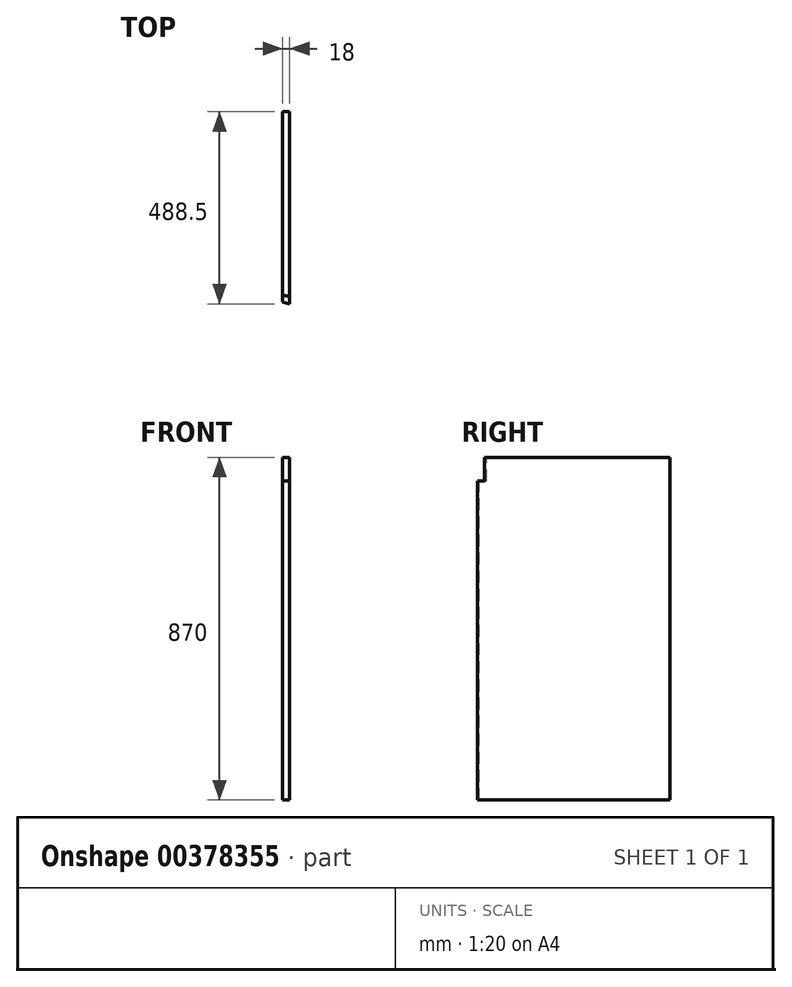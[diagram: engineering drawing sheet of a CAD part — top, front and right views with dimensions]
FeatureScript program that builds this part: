
annotation { "Feature Type Name" : "Feature", "Feature Type Description" : "" }
export const myFeature = defineFeature(function(context is Context, id is Id, definition is map)
    precondition{}
    {
        {
            var Q0;
            Q0=qCreatedBy(makeId("Right.planeOp"),FACE);
            var sketch = newSketch(context, id + "F0", { "sketchPlane" : qUnion([Q0])});
            skLineSegment(sketch, "E0.bottom", {"start": v(244.25, 435) * mm, "end": v(-244.25, 435) * mm});
            skLineSegment(sketch, "E0.top", {"start": v(244.25, -435) * mm, "end": v(-244.25, -435) * mm});
            skLineSegment(sketch, "E0.left", {"start": v(244.25, 435) * mm, "end": v(244.25, -435) * mm});
            skLineSegment(sketch, "E0.right", {"start": v(-244.25, 435) * mm, "end": v(-244.25, -435) * mm});
            skPoint(sketch, "E0.middle", {"position": v(0, 0) * mm});
            skSolve(sketch);
        }
        {
            var Q0;
            Q0 = qSketchRegion(id + "F0", true);
            extrude(context, id + "F1", {"entities" : qUnion([Q0]), "depth" : 18 * mm});
        }
        {
            var Q0;
            Q0=makeQuery(id+"F1.opExtrude","SWEPT_FACE",FACE,{"disambiguationData":[OSD([sQuery(id+"F0.wireOp",EDGE,"E0.bottom")])]});
            var sketch = newSketch(context, id + "F2", { "sketchPlane" : qUnion([Q0])});
            skLineSegment(sketch, "E1", {"start": v(18, -244.25) * mm, "end": v(0, -239.76) * mm});
            skLineSegment(sketch, "E2", {"start": v(0, -239.76) * mm, "end": v(0, -244.25) * mm});
            skLineSegment(sketch, "E3", {"start": v(0, -244.25) * mm, "end": v(18, -244.25) * mm});
            skSolve(sketch);
        }
        {
            var Q0;
            Q0 = qSketchRegion(id + "F2", true);
            extrude(context, id + "F3", {"entities" : qUnion([Q0]), "operationType" : NewBodyOperationType.REMOVE, "oppositeDirection" : true, "depth" : 870 * mm});
        }
        {
            var Q0;
            Q0=makeQuery(id+"F1.opExtrude","SWEPT_FACE",FACE,{"disambiguationData":[OSD([sQuery(id+"F0.wireOp",EDGE,"E0.bottom")])]});
            var sketch = newSketch(context, id + "F4", { "sketchPlane" : qUnion([Q0])});
            skLineSegment(sketch, "E4", {"start": v(0, -239.76) * mm, "end": v(18, -244.25) * mm});
            skLineSegment(sketch, "E5", {"start": v(18, -244.25) * mm, "end": v(18, -225.7) * mm});
            skLineSegment(sketch, "E6", {"start": v(18, -225.7) * mm, "end": v(0, -221.21) * mm});
            skLineSegment(sketch, "E7", {"start": v(0, -221.21) * mm, "end": v(0, -239.76) * mm});
            skSolve(sketch);
        }
        {
            var Q0;
            Q0 = qSketchRegion(id + "F4", true);
            extrude(context, id + "F5", {"entities" : qUnion([Q0]), "operationType" : NewBodyOperationType.REMOVE, "oppositeDirection" : true, "depth" : 60 * mm});
        }
    });
